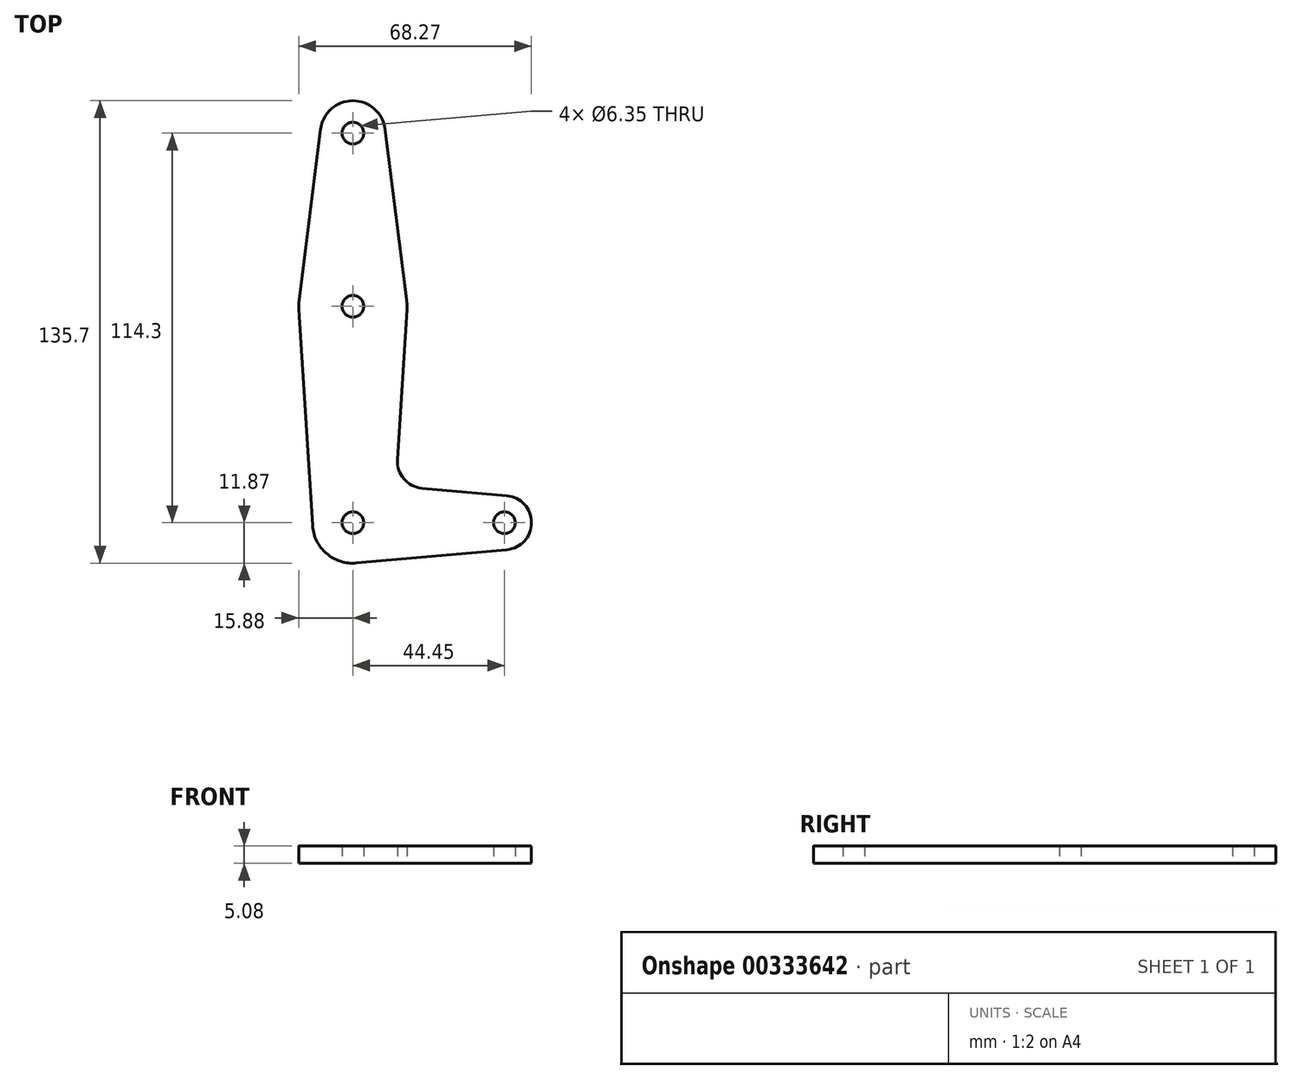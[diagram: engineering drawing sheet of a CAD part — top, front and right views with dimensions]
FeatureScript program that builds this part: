
annotation { "Feature Type Name" : "Feature", "Feature Type Description" : "" }
export const myFeature = defineFeature(function(context is Context, id is Id, definition is map)
    precondition{}
    {
        {
            var Q0;
            Q0=qCreatedBy(makeId("Top.planeOp"),FACE);
            var sketch = newSketch(context, id + "F0", { "sketchPlane" : qUnion([Q0])});
            skLineSegment(sketch, "E0", {"start": v(0, 88.16) * mm, "end": v(0, -26.14) * mm, "construction": true});
            skLineSegment(sketch, "E1", {"start": v(0, -26.14) * mm, "end": v(44.45, -26.14) * mm, "construction": true});
            skCircle(sketch, "E2", {"center": v(0, 88.16) * mm, "radius": 9.53 * mm});
            skCircle(sketch, "E3", {"center": v(0, -26.14) * mm, "radius": 11.87 * mm});
            skCircle(sketch, "E4", {"center": v(0, 37.36) * mm, "radius": 15.88 * mm});
            skCircle(sketch, "E5", {"center": v(44.45, -26.14) * mm, "radius": 7.94 * mm});
            skLineSegment(sketch, "E6", {"start": v(-9.45, 89.35) * mm, "end": v(-15.75, 39.34) * mm});
            skLineSegment(sketch, "E7", {"start": v(9.45, 89.35) * mm, "end": v(15.75, 39.34) * mm});
            skLineSegment(sketch, "E8", {"start": v(15.84, 36.36) * mm, "end": v(13.07, -7.6) * mm});
            skLineSegment(sketch, "E9", {"start": v(20.3, -16.02) * mm, "end": v(45.15, -18.23) * mm});
            skLineSegment(sketch, "E10", {"start": v(45.15, -34.05) * mm, "end": v(1.05, -37.97) * mm});
            skLineSegment(sketch, "E11", {"start": v(-15.84, 36.36) * mm, "end": v(-11.85, -26.89) * mm});
            skCircle(sketch, "E12", {"center": v(0, 88.16) * mm, "radius": 3.18 * mm});
            skCircle(sketch, "E13", {"center": v(0, 37.36) * mm, "radius": 3.18 * mm});
            skCircle(sketch, "E14", {"center": v(0, -26.14) * mm, "radius": 3.18 * mm});
            skCircle(sketch, "E15", {"center": v(44.45, -26.14) * mm, "radius": 3.18 * mm});
            skArc(sketch, "E16.filletArc", {"start": v(13.07, -7.6) * mm, "mid": v(14.97, -13.28) * mm, "end": v(20.3, -16.02) * mm});
            skSolve(sketch);
        }
        {
            var Q0;
            Q0 = qSketchRegion(id + "F0", true);
            extrude(context, id + "F1", {"entities" : qUnion([Q0]), "depth" : 5.08 * mm});
        }
    });
